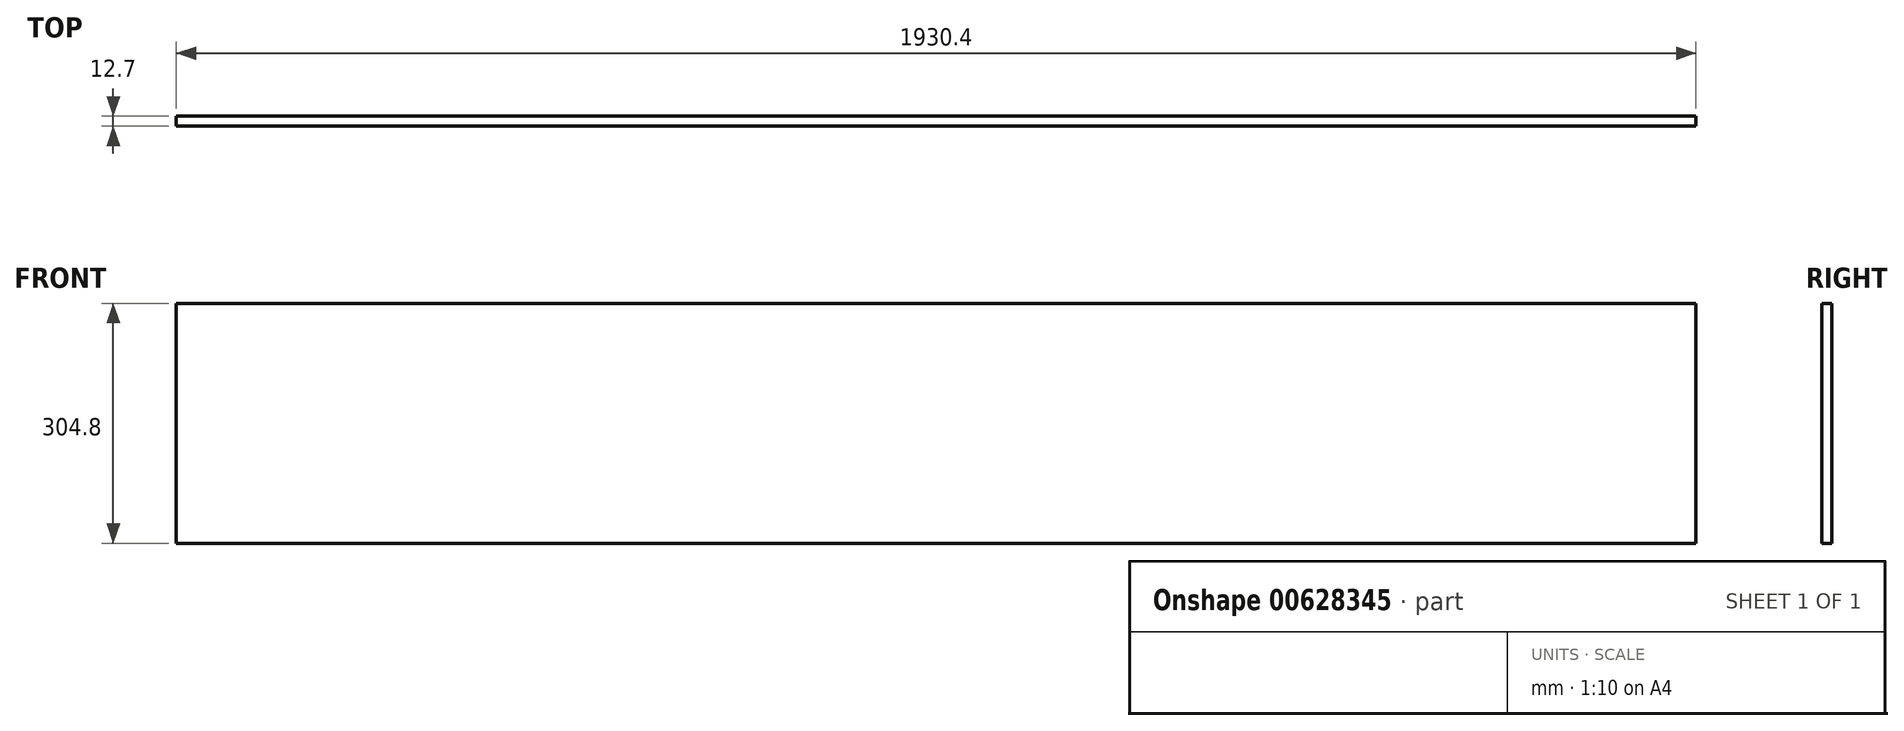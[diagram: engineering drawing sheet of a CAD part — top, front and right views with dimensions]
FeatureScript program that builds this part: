
annotation { "Feature Type Name" : "Feature", "Feature Type Description" : "" }
export const myFeature = defineFeature(function(context is Context, id is Id, definition is map)
    precondition{}
    {
        {
            var Q0;
            Q0=qCreatedBy(makeId("Front.planeOp"),FACE);
            var sketch = newSketch(context, id + "F0", { "sketchPlane" : qUnion([Q0])});
            skLineSegment(sketch, "E0.bottom", {"start": v(0, 0) * mm, "end": v(1930.4, 0) * mm});
            skLineSegment(sketch, "E0.top", {"start": v(0, 304.8) * mm, "end": v(1930.4, 304.8) * mm});
            skLineSegment(sketch, "E0.left", {"start": v(0, 0) * mm, "end": v(0, 304.8) * mm});
            skLineSegment(sketch, "E0.right", {"start": v(1930.4, 0) * mm, "end": v(1930.4, 304.8) * mm});
            skSolve(sketch);
        }
        {
            var Q0;
            Q0 = qSketchRegion(id + "F0", true);
            extrude(context, id + "F1", {"entities" : qUnion([Q0]), "depth" : 12.7 * mm, "offsetDistance" : 25.4 * mm});
        }
    });
